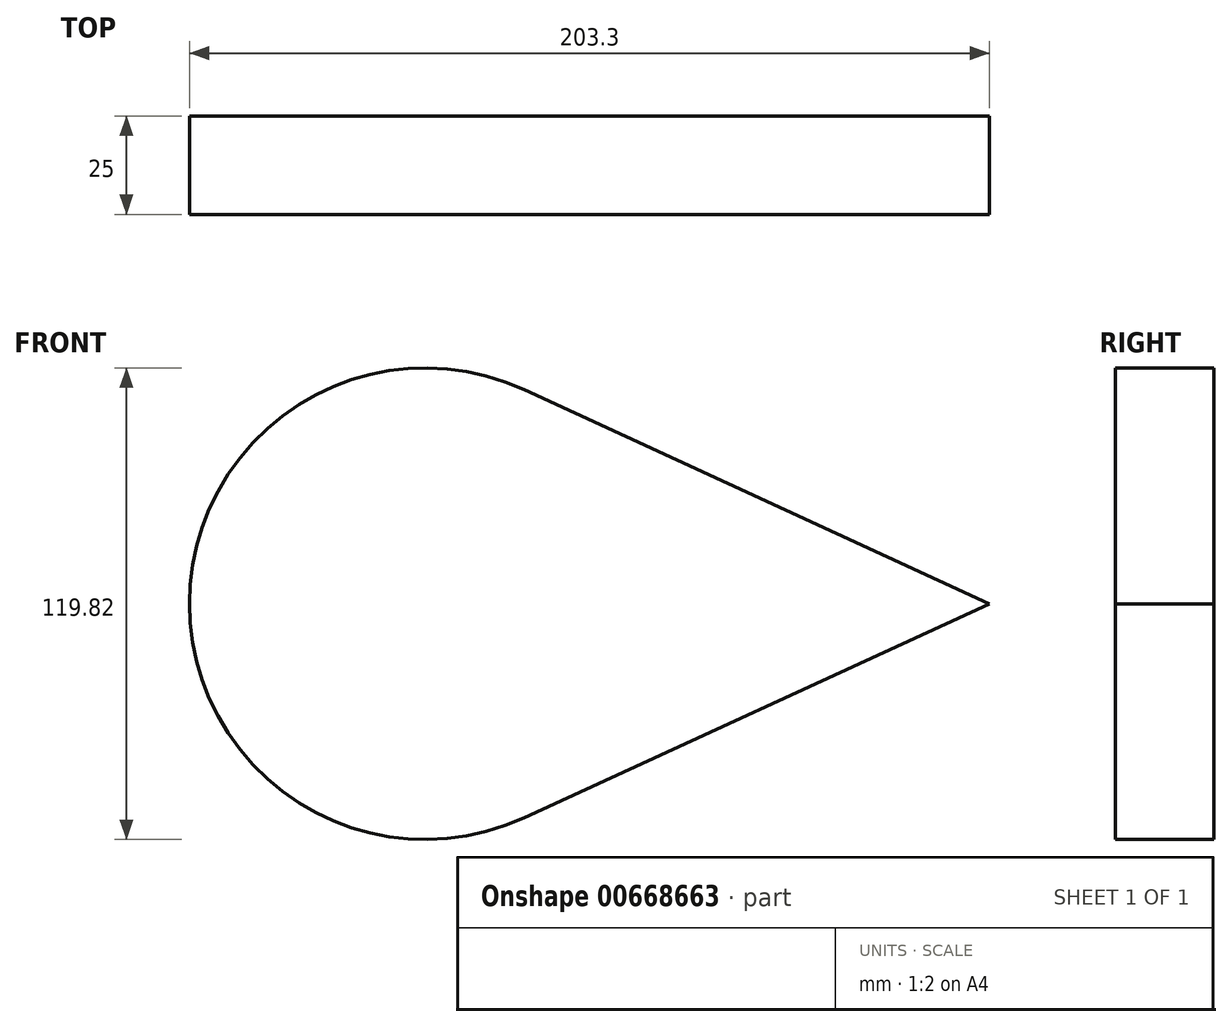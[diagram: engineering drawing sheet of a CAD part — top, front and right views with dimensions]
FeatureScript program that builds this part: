
annotation { "Feature Type Name" : "Feature", "Feature Type Description" : "" }
export const myFeature = defineFeature(function(context is Context, id is Id, definition is map)
    precondition{}
    {
        {
            var Q0;
            Q0=qCreatedBy(makeId("Front.planeOp"),FACE);
            var sketch = newSketch(context, id + "F0", { "sketchPlane" : qUnion([Q0])});
            skCircle(sketch, "E0", {"center": v(-50.4, 0) * mm, "radius": 59.91 * mm});
            skLineSegment(sketch, "E1", {"start": v(92.99, 0) * mm, "end": v(-25.37, -54.43) * mm});
            skLineSegment(sketch, "E2", {"start": v(92.99, 0) * mm, "end": v(-25.37, 54.43) * mm});
            skSolve(sketch);
        }
        {
            var Q0;
            Q0 = qSketchRegion(id + "F0", true);
            extrude(context, id + "F1", {"entities" : qUnion([Q0]), "depth" : 25 * mm, "offsetDistance" : 25 * mm});
        }
    });
